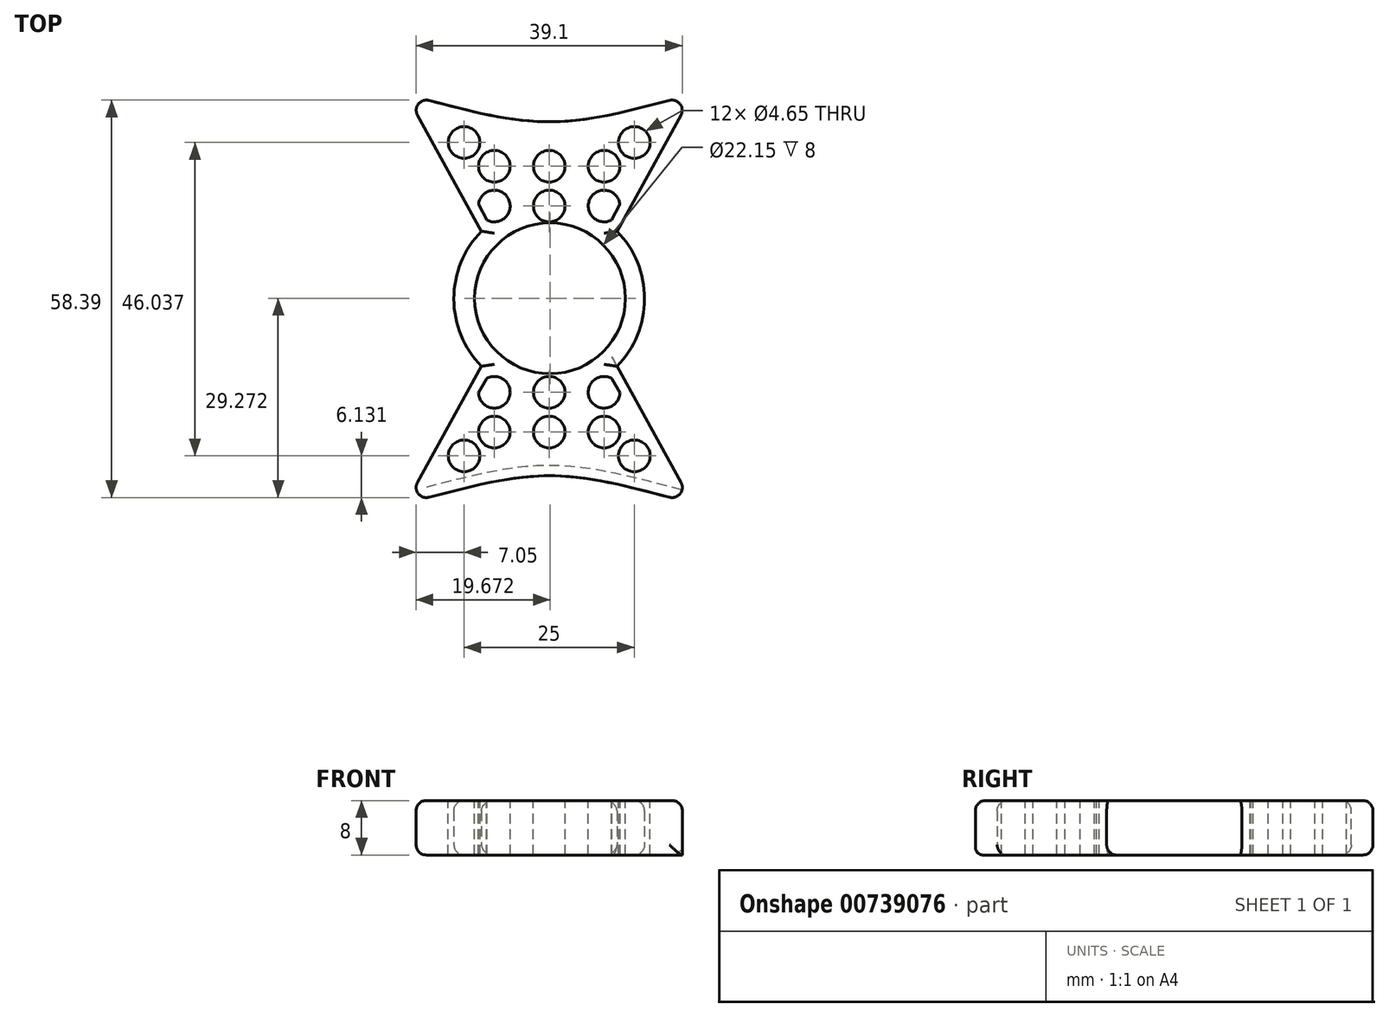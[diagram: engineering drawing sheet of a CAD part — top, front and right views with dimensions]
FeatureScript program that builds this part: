
annotation { "Feature Type Name" : "Feature", "Feature Type Description" : "" }
export const myFeature = defineFeature(function(context is Context, id is Id, definition is map)
    precondition{}
    {
        {
            var Q0;
            Q0=qCreatedBy(makeId("Top.planeOp"),FACE);
            var sketch = newSketch(context, id + "F0", { "sketchPlane" : qUnion([Q0])});
            skCircle(sketch, "E0", {"center": v(0, 0) * mm, "radius": 14 * mm});
            skLineSegment(sketch, "E1", {"start": v(-14, 0) * mm, "end": v(0, 0) * mm});
            skLineSegment(sketch, "E2", {"start": v(-9.9, 9.9) * mm, "end": v(0, 0) * mm});
            skLineSegment(sketch, "E3", {"start": v(9.9, 9.9) * mm, "end": v(0, 0) * mm});
            skLineSegment(sketch, "E4", {"start": v(0, 0) * mm, "end": v(14, 0) * mm});
            skLineSegment(sketch, "E5", {"start": v(-9.9, 9.9) * mm, "end": v(-21.01, 30.04) * mm});
            skLineSegment(sketch, "E6", {"start": v(9.9, 9.9) * mm, "end": v(21.01, 30.04) * mm});
            skFitSpline(sketch, "E7", {"points": [v(-21.01, 30.04) * mm, v(0, 26.06) * mm, v(21.01, 30.04) * mm], "startDerivative": vector(39.9, -9.48) * mm, "endDerivative": vector(39.9, 9.48) * mm});
            skCircle(sketch, "E8.1.0", {"center": v(0, 0.12) * mm, "radius": 14 * mm});
            skLineSegment(sketch, "E8.1.1", {"start": v(14, 0.12) * mm, "end": v(0, 0.12) * mm});
            skLineSegment(sketch, "E8.1.2", {"start": v(-9.9, -9.78) * mm, "end": v(-21.01, -29.91) * mm});
            skLineSegment(sketch, "E8.1.3", {"start": v(9.9, -9.78) * mm, "end": v(21.01, -29.91) * mm});
            skLineSegment(sketch, "E8.1.4", {"start": v(9.9, -9.78) * mm, "end": v(0, 0.12) * mm});
            skLineSegment(sketch, "E8.1.5", {"start": v(-9.9, -9.78) * mm, "end": v(0, 0.12) * mm});
            skLineSegment(sketch, "E8.1.6", {"start": v(0, 0.12) * mm, "end": v(-14, 0.12) * mm});
            skPoint(sketch, "E8.center", {"position": v(0, 0.06) * mm});
            skFitSpline(sketch, "E9", {"points": [v(-21.01, -29.91) * mm, v(0, -25.94) * mm, v(21.01, -29.91) * mm], "startDerivative": vector(39.9, 9.1) * mm, "endDerivative": vector(39.9, -9.1) * mm});
            skSolve(sketch);
        }
        {
            var Q0;
            Q0 = qSketchRegion(id + "F0", true);
            var Q1;
            {var subQ1=sQuery(id+"F0.wireOp",EDGE,"E0");var subQ3=sQuery(id+"F0.wireOp",EDGE,"E8.1.1");var subQ4=makeQuery(id+"F0.imprint","INTERSECT",VERTEX,{"derivedFrom":[subQ1,subQ3]});Q1=makeQuery(id+"F0.imprint","IMPRINT",FACE,{"disambiguationData":[TD([[makeQuery(id+"F0.imprint","IMPRINT",EDGE,{"disambiguationData":[TD([[subQ4,-1.0]])],"derivedFrom":subQ3}),-1.0]])]});}
            var Q2;
            {var subQ0=sQuery(id+"F0.wireOp",EDGE,"E8.1.6");var subQ5=sQuery(id+"F0.wireOp",EDGE,"E2");var subQ6=makeQuery(id+"F0.imprint","INTERSECT",VERTEX,{"derivedFrom":[subQ5,subQ0]});Q2=makeQuery(id+"F0.imprint","IMPRINT",FACE,{"disambiguationData":[TD([[makeQuery(id+"F0.imprint","IMPRINT",EDGE,{"disambiguationData":[TD([[subQ6,1.0]])],"derivedFrom":subQ5}),1.0]])]});}
            var Q3;
            {var subQ1=sQuery(id+"F0.wireOp",EDGE,"E0");var subQ3=sQuery(id+"F0.wireOp",EDGE,"E8.1.6");var subQ4=makeQuery(id+"F0.imprint","INTERSECT",VERTEX,{"derivedFrom":[subQ1,subQ3]});Q3=makeQuery(id+"F0.imprint","IMPRINT",FACE,{"disambiguationData":[TD([[makeQuery(id+"F0.imprint","IMPRINT",EDGE,{"disambiguationData":[TD([[subQ4,1.0]])],"derivedFrom":subQ3}),-1.0]])]});}
            var Q4;
            {var subQ0=sQuery(id+"F0.wireOp",EDGE,"E8.1.0");var subQ1=sQuery(id+"F0.wireOp",EDGE,"E1");var subQ2=makeQuery(id+"F0.imprint","INTERSECT",VERTEX,{"derivedFrom":[subQ1,subQ0]});Q4=makeQuery(id+"F0.imprint","IMPRINT",FACE,{"disambiguationData":[TD([[makeQuery(id+"F0.imprint","IMPRINT",EDGE,{"disambiguationData":[TD([[subQ2,-1.0]])],"derivedFrom":subQ1}),-1.0]])]});}
            var Q5;
            {var subQ0=sQuery(id+"F0.wireOp",EDGE,"E8.1.4");var subQ1=sQuery(id+"F0.wireOp",EDGE,"E4");var subQ2=makeQuery(id+"F0.imprint","INTERSECT",VERTEX,{"derivedFrom":[subQ1,subQ0]});Q5=makeQuery(id+"F0.imprint","IMPRINT",FACE,{"disambiguationData":[TD([[makeQuery(id+"F0.imprint","IMPRINT",EDGE,{"disambiguationData":[TD([[subQ2,-1.0]])],"derivedFrom":subQ1}),-1.0]])]});}
            var Q6;
            {var subQ3=sQuery(id+"F0.wireOp",EDGE,"E8.1.4");var subQ5=sQuery(id+"F0.wireOp",EDGE,"E4");var subQ8=makeQuery(id+"F0.imprint","INTERSECT",VERTEX,{"derivedFrom":[subQ5,subQ3]});Q6=makeQuery(id+"F0.imprint","IMPRINT",FACE,{"disambiguationData":[TD([[makeQuery(id+"F0.imprint","IMPRINT",EDGE,{"disambiguationData":[TD([[subQ8,1.0]])],"derivedFrom":subQ3}),1.0]])]});}
            extrude(context, id + "F1", {"entities" : qUnion([Q0, Q1, Q2, Q3, Q4, Q5, Q6]), "depth" : 8 * mm, "offsetDistance" : 25 * mm});
        }
        {
            var Q0;
            Q0=makeQuery(id+"F1.opExtrude","SWEPT_EDGE",EDGE,{"disambiguationData":[OSD([sQuery(id+"F0.wireOp",EDGE,"E8.1.2"),sQuery(id+"F0.wireOp",EDGE,"E9")])]});
            var Q1;
            Q1=makeQuery(id+"F1.opExtrude","CAP_EDGE",EDGE,{"disambiguationData":[OSD([sQuery(id+"F0.wireOp",EDGE,"E9")])],"isStart":true});
            var Q2;
            Q2=makeQuery(id+"F1.opExtrude","CAP_EDGE",EDGE,{"disambiguationData":[OSD([sQuery(id+"F0.wireOp",EDGE,"E9")])],"isStart":false});
            var Q3;
            Q3=makeQuery(id+"F1.opExtrude","CAP_EDGE",EDGE,{"disambiguationData":[OSD([sQuery(id+"F0.wireOp",EDGE,"E8.1.2")])],"isStart":false});
            var Q4;
            {var subQ0=sQuery(id+"F0.wireOp",EDGE,"E0");var subQ1=makeQuery(id+"F0.imprint","INTERSECT",VERTEX,{"derivedFrom":[subQ0,sQuery(id+"F0.wireOp",EDGE,"E1")]});Q4=makeQuery(id+"F1.opExtrude","CAP_EDGE",EDGE,{"disambiguationData":[OSD([subQ0]),TDD([makeQuery(id+"F0.imprint","IMPRINT",EDGE,{"disambiguationData":[TD([[subQ1,1.0]])],"derivedFrom":subQ0}),makeQuery(id+"F0.imprint","IMPRINT",EDGE,{"disambiguationData":[TD([[subQ1,-1.0]])],"derivedFrom":subQ0})])],"isStart":false});}
            var Q5;
            {var subQ0=sQuery(id+"F0.wireOp",EDGE,"E8.1.0");var subQ1=makeQuery(id+"F0.imprint","INTERSECT",VERTEX,{"derivedFrom":[subQ0,sQuery(id+"F0.wireOp",EDGE,"E8.1.6")]});Q5=makeQuery(id+"F1.opExtrude","CAP_EDGE",EDGE,{"disambiguationData":[OSD([subQ0]),TDD([makeQuery(id+"F0.imprint","IMPRINT",EDGE,{"disambiguationData":[TD([[subQ1,-1.0]])],"derivedFrom":subQ0}),makeQuery(id+"F0.imprint","IMPRINT",EDGE,{"disambiguationData":[TD([[subQ1,1.0]])],"derivedFrom":subQ0})])],"isStart":false});}
            var Q6;
            Q6=makeQuery(id+"F1.opExtrude","CAP_EDGE",EDGE,{"disambiguationData":[OSD([sQuery(id+"F0.wireOp",EDGE,"E5")])],"isStart":false});
            var Q7;
            Q7=makeQuery(id+"F1.opExtrude","CAP_EDGE",EDGE,{"disambiguationData":[OSD([sQuery(id+"F0.wireOp",EDGE,"E7")])],"isStart":false});
            var Q8;
            Q8=makeQuery(id+"F1.opExtrude","CAP_EDGE",EDGE,{"disambiguationData":[OSD([sQuery(id+"F0.wireOp",EDGE,"E6")])],"isStart":false});
            var Q9;
            Q9=makeQuery(id+"F1.opExtrude","SWEPT_EDGE",EDGE,{"disambiguationData":[OSD([sQuery(id+"F0.wireOp",EDGE,"E6"),sQuery(id+"F0.wireOp",EDGE,"E7")])]});
            var Q10;
            Q10=makeQuery(id+"F1.opExtrude","CAP_EDGE",EDGE,{"disambiguationData":[OSD([sQuery(id+"F0.wireOp",EDGE,"E6")])],"isStart":true});
            var Q11;
            {var subQ0=sQuery(id+"F0.wireOp",EDGE,"E0");var subQ1=makeQuery(id+"F0.imprint","INTERSECT",VERTEX,{"derivedFrom":[subQ0,sQuery(id+"F0.wireOp",EDGE,"E4")]});Q11=makeQuery(id+"F1.opExtrude","CAP_EDGE",EDGE,{"disambiguationData":[OSD([subQ0]),TDD([makeQuery(id+"F0.imprint","IMPRINT",EDGE,{"disambiguationData":[TD([[subQ1,-1.0]])],"derivedFrom":subQ0}),makeQuery(id+"F0.imprint","IMPRINT",EDGE,{"disambiguationData":[TD([[subQ1,1.0]])],"derivedFrom":subQ0})])],"isStart":true});}
            var Q12;
            {var subQ0=sQuery(id+"F0.wireOp",EDGE,"E8.1.0");var subQ1=makeQuery(id+"F0.imprint","INTERSECT",VERTEX,{"derivedFrom":[subQ0,sQuery(id+"F0.wireOp",EDGE,"E8.1.1")]});Q12=makeQuery(id+"F1.opExtrude","CAP_EDGE",EDGE,{"disambiguationData":[OSD([subQ0]),TDD([makeQuery(id+"F0.imprint","IMPRINT",EDGE,{"disambiguationData":[TD([[subQ1,1.0]])],"derivedFrom":subQ0}),makeQuery(id+"F0.imprint","IMPRINT",EDGE,{"disambiguationData":[TD([[subQ1,-1.0]])],"derivedFrom":subQ0})])],"isStart":true});}
            var Q13;
            {var subQ0=sQuery(id+"F0.wireOp",EDGE,"E8.1.0");var subQ1=makeQuery(id+"F0.imprint","INTERSECT",VERTEX,{"derivedFrom":[subQ0,sQuery(id+"F0.wireOp",EDGE,"E8.1.1")]});Q13=makeQuery(id+"F1.opExtrude","CAP_EDGE",EDGE,{"disambiguationData":[OSD([subQ0]),TDD([makeQuery(id+"F0.imprint","IMPRINT",EDGE,{"disambiguationData":[TD([[subQ1,1.0]])],"derivedFrom":subQ0}),makeQuery(id+"F0.imprint","IMPRINT",EDGE,{"disambiguationData":[TD([[subQ1,-1.0]])],"derivedFrom":subQ0})])],"isStart":false});}
            var Q14;
            Q14=makeQuery(id+"F1.opExtrude","CAP_EDGE",EDGE,{"disambiguationData":[OSD([sQuery(id+"F0.wireOp",EDGE,"E8.1.3")])],"isStart":false});
            var Q15;
            {var subQ0=sQuery(id+"F0.wireOp",EDGE,"E0");var subQ1=makeQuery(id+"F0.imprint","INTERSECT",VERTEX,{"derivedFrom":[subQ0,sQuery(id+"F0.wireOp",EDGE,"E4")]});Q15=makeQuery(id+"F1.opExtrude","CAP_EDGE",EDGE,{"disambiguationData":[OSD([subQ0]),TDD([makeQuery(id+"F0.imprint","IMPRINT",EDGE,{"disambiguationData":[TD([[subQ1,-1.0]])],"derivedFrom":subQ0}),makeQuery(id+"F0.imprint","IMPRINT",EDGE,{"disambiguationData":[TD([[subQ1,1.0]])],"derivedFrom":subQ0})])],"isStart":false});}
            var Q16;
            Q16=makeQuery(id+"F1.opExtrude","CAP_EDGE",EDGE,{"disambiguationData":[OSD([sQuery(id+"F0.wireOp",EDGE,"E5")])],"isStart":true});
            var Q17;
            Q17=makeQuery(id+"F1.opExtrude","CAP_EDGE",EDGE,{"disambiguationData":[OSD([sQuery(id+"F0.wireOp",EDGE,"E7")])],"isStart":true});
            var Q18;
            {var subQ0=sQuery(id+"F0.wireOp",EDGE,"E8.1.0");var subQ1=makeQuery(id+"F0.imprint","INTERSECT",VERTEX,{"derivedFrom":[subQ0,sQuery(id+"F0.wireOp",EDGE,"E8.1.6")]});Q18=makeQuery(id+"F1.opExtrude","CAP_EDGE",EDGE,{"disambiguationData":[OSD([subQ0]),TDD([makeQuery(id+"F0.imprint","IMPRINT",EDGE,{"disambiguationData":[TD([[subQ1,-1.0]])],"derivedFrom":subQ0}),makeQuery(id+"F0.imprint","IMPRINT",EDGE,{"disambiguationData":[TD([[subQ1,1.0]])],"derivedFrom":subQ0})])],"isStart":true});}
            var Q19;
            {var subQ0=sQuery(id+"F0.wireOp",EDGE,"E0");var subQ1=makeQuery(id+"F0.imprint","INTERSECT",VERTEX,{"derivedFrom":[subQ0,sQuery(id+"F0.wireOp",EDGE,"E1")]});Q19=makeQuery(id+"F1.opExtrude","CAP_EDGE",EDGE,{"disambiguationData":[OSD([subQ0]),TDD([makeQuery(id+"F0.imprint","IMPRINT",EDGE,{"disambiguationData":[TD([[subQ1,1.0]])],"derivedFrom":subQ0}),makeQuery(id+"F0.imprint","IMPRINT",EDGE,{"disambiguationData":[TD([[subQ1,-1.0]])],"derivedFrom":subQ0})])],"isStart":true});}
            var Q20;
            Q20=makeQuery(id+"F1.opExtrude","CAP_EDGE",EDGE,{"disambiguationData":[OSD([sQuery(id+"F0.wireOp",EDGE,"E8.1.2")])],"isStart":true});
            var Q21;
            Q21=makeQuery(id+"F1.opExtrude","SWEPT_EDGE",EDGE,{"disambiguationData":[OSD([sQuery(id+"F0.wireOp",EDGE,"E8.1.3"),sQuery(id+"F0.wireOp",EDGE,"E9")])]});
            var Q22;
            Q22=makeQuery(id+"F1.opExtrude","SWEPT_EDGE",EDGE,{"disambiguationData":[OSD([sQuery(id+"F0.wireOp",EDGE,"E5"),sQuery(id+"F0.wireOp",EDGE,"E7")])]});
            fillet(context, id + "F2", {"entities" : qUnion([Q0, Q1, Q2, Q3, Q4, Q5, Q6, Q7, Q8, Q9, Q10, Q11, Q12, Q13, Q14, Q15, Q16, Q17, Q18, Q19, Q20, Q21, Q22]), "radius" : 1.5 * mm, "tangentPropagation" : true, "allowEdgeOverflow" : false});
        }
        {
            var Q0;
            Q0=makeQuery(id+"F1.opExtrude","CAP_FACE",FACE,{"disambiguationData":[OSD([sQuery(id+"F0.wireOp",EDGE,"E0"),sQuery(id+"F0.wireOp",EDGE,"E1"),sQuery(id+"F0.wireOp",EDGE,"E2"),sQuery(id+"F0.wireOp",EDGE,"E3"),sQuery(id+"F0.wireOp",EDGE,"E4"),sQuery(id+"F0.wireOp",EDGE,"E5"),sQuery(id+"F0.wireOp",EDGE,"E6"),sQuery(id+"F0.wireOp",EDGE,"E7"),sQuery(id+"F0.wireOp",EDGE,"E8.1.0"),sQuery(id+"F0.wireOp",EDGE,"E8.1.1"),sQuery(id+"F0.wireOp",EDGE,"E8.1.2"),sQuery(id+"F0.wireOp",EDGE,"E8.1.3"),sQuery(id+"F0.wireOp",EDGE,"E8.1.4"),sQuery(id+"F0.wireOp",EDGE,"E8.1.5"),sQuery(id+"F0.wireOp",EDGE,"E8.1.6"),sQuery(id+"F0.wireOp",EDGE,"E9")])],"isStart":false});
            var sketch = newSketch(context, id + "F3", { "sketchPlane" : qUnion([Q0])});
            skCircle(sketch, "E10", {"center": v(0.12, 0.12) * mm, "radius": 11.07 * mm});
            skCircle(sketch, "E11", {"center": v(0, -13.68) * mm, "radius": 2.33 * mm});
            skCircle(sketch, "E12", {"center": v(0, -19.52) * mm, "radius": 2.33 * mm});
            skCircle(sketch, "E13", {"center": v(8.06, -19.52) * mm, "radius": 2.33 * mm});
            skCircle(sketch, "E14", {"center": v(-8.06, -19.52) * mm, "radius": 2.33 * mm});
            skCircle(sketch, "E15", {"center": v(-8.06, -13.68) * mm, "radius": 2.33 * mm});
            skCircle(sketch, "E16", {"center": v(8.06, -13.68) * mm, "radius": 2.33 * mm});
            skCircle(sketch, "E17", {"center": v(-12.5, -23.02) * mm, "radius": 2.33 * mm});
            skPoint(sketch, "E18.centerSnap0", {"position": v(11.35, -5.24) * mm});
            skCircle(sketch, "E19", {"center": v(12.5, -23.02) * mm, "radius": 2.33 * mm});
            skCircle(sketch, "E20.1.0", {"center": v(0, 19.52) * mm, "radius": 2.33 * mm});
            skCircle(sketch, "E20.1.1", {"center": v(8.06, 19.52) * mm, "radius": 2.33 * mm});
            skCircle(sketch, "E20.1.2", {"center": v(12.5, 23.02) * mm, "radius": 2.33 * mm});
            skCircle(sketch, "E20.1.3", {"center": v(8.06, 13.68) * mm, "radius": 2.33 * mm});
            skCircle(sketch, "E20.1.4", {"center": v(0, 13.68) * mm, "radius": 2.33 * mm});
            skCircle(sketch, "E20.1.5", {"center": v(-8.06, 13.68) * mm, "radius": 2.33 * mm});
            skCircle(sketch, "E20.1.6", {"center": v(-8.06, 19.52) * mm, "radius": 2.33 * mm});
            skCircle(sketch, "E20.1.7", {"center": v(-12.5, 23.02) * mm, "radius": 2.33 * mm});
            skPoint(sketch, "E20.center", {"position": v(0, 0) * mm});
            skSolve(sketch);
        }
        {
            var Q0;
            Q0=makeQuery(id+"F3.imprint","IMPRINT",FACE,{"disambiguationData":[TD([[makeQuery(id+"F3.imprint","IMPRINT",EDGE,{"derivedFrom":sQuery(id+"F3.wireOp",EDGE,"E17")}),1.0]])]});
            var Q1;
            Q1=makeQuery(id+"F3.imprint","IMPRINT",FACE,{"disambiguationData":[TD([[makeQuery(id+"F3.imprint","IMPRINT",EDGE,{"derivedFrom":sQuery(id+"F3.wireOp",EDGE,"E14")}),1.0]])]});
            var Q2;
            {var subQ0=sQuery(id+"F3.wireOp",EDGE,"E15");var subQ1=sQuery(id+"F0.wireOp",EDGE,"E8.1.2");var subQ2=makeQuery(id+"F2.opFillet","BLEND_EDGE",EDGE,{"blendedFrom":[makeQuery(id+"F1.opExtrude","CAP_EDGE",EDGE,{"disambiguationData":[OSD([subQ1])],"isStart":false}),makeQuery(id+"F1.opExtrude","CAP_FACE",FACE,{"disambiguationData":[OSD([sQuery(id+"F0.wireOp",EDGE,"E0"),sQuery(id+"F0.wireOp",EDGE,"E1"),sQuery(id+"F0.wireOp",EDGE,"E2"),sQuery(id+"F0.wireOp",EDGE,"E3"),sQuery(id+"F0.wireOp",EDGE,"E4"),sQuery(id+"F0.wireOp",EDGE,"E5"),sQuery(id+"F0.wireOp",EDGE,"E6"),sQuery(id+"F0.wireOp",EDGE,"E7"),sQuery(id+"F0.wireOp",EDGE,"E8.1.0"),sQuery(id+"F0.wireOp",EDGE,"E8.1.1"),subQ1,sQuery(id+"F0.wireOp",EDGE,"E8.1.3"),sQuery(id+"F0.wireOp",EDGE,"E8.1.4"),sQuery(id+"F0.wireOp",EDGE,"E8.1.5"),sQuery(id+"F0.wireOp",EDGE,"E8.1.6"),sQuery(id+"F0.wireOp",EDGE,"E9")])],"isStart":false})],"blendedInto":[makeQuery(id+"F1.opExtrude","CAP_FACE",FACE,{"disambiguationData":[OSD([sQuery(id+"F0.wireOp",EDGE,"E0"),sQuery(id+"F0.wireOp",EDGE,"E1"),sQuery(id+"F0.wireOp",EDGE,"E2"),sQuery(id+"F0.wireOp",EDGE,"E3"),sQuery(id+"F0.wireOp",EDGE,"E4"),sQuery(id+"F0.wireOp",EDGE,"E5"),sQuery(id+"F0.wireOp",EDGE,"E6"),sQuery(id+"F0.wireOp",EDGE,"E7"),sQuery(id+"F0.wireOp",EDGE,"E8.1.0"),sQuery(id+"F0.wireOp",EDGE,"E8.1.1"),subQ1,sQuery(id+"F0.wireOp",EDGE,"E8.1.3"),sQuery(id+"F0.wireOp",EDGE,"E8.1.4"),sQuery(id+"F0.wireOp",EDGE,"E8.1.5"),sQuery(id+"F0.wireOp",EDGE,"E8.1.6"),sQuery(id+"F0.wireOp",EDGE,"E9")])],"isStart":false})]});var subQ3=makeQuery(id+"F3.imprint","INTERSECT",VERTEX,{"disambiguationData":[OD(0.0)],"derivedFrom":[subQ2,subQ0]});Q2=makeQuery(id+"F3.imprint","IMPRINT",FACE,{"disambiguationData":[TD([[makeQuery(id+"F3.imprint","IMPRINT",EDGE,{"disambiguationData":[TD([[subQ3,-1.0]])],"derivedFrom":subQ0}),1.0]])]});}
            var Q3;
            Q3=makeQuery(id+"F3.imprint","IMPRINT",FACE,{"disambiguationData":[TD([[makeQuery(id+"F3.imprint","IMPRINT",EDGE,{"derivedFrom":sQuery(id+"F3.wireOp",EDGE,"E12")}),1.0]])]});
            var Q4;
            Q4=makeQuery(id+"F3.imprint","IMPRINT",FACE,{"disambiguationData":[TD([[makeQuery(id+"F3.imprint","IMPRINT",EDGE,{"derivedFrom":sQuery(id+"F3.wireOp",EDGE,"E11")}),1.0]])]});
            var Q5;
            {var subQ0=sQuery(id+"F3.wireOp",EDGE,"E16");var subQ1=sQuery(id+"F0.wireOp",EDGE,"E8.1.3");var subQ2=makeQuery(id+"F2.opFillet","BLEND_EDGE",EDGE,{"blendedFrom":[makeQuery(id+"F1.opExtrude","CAP_EDGE",EDGE,{"disambiguationData":[OSD([subQ1])],"isStart":false}),makeQuery(id+"F1.opExtrude","CAP_FACE",FACE,{"disambiguationData":[OSD([sQuery(id+"F0.wireOp",EDGE,"E0"),sQuery(id+"F0.wireOp",EDGE,"E1"),sQuery(id+"F0.wireOp",EDGE,"E2"),sQuery(id+"F0.wireOp",EDGE,"E3"),sQuery(id+"F0.wireOp",EDGE,"E4"),sQuery(id+"F0.wireOp",EDGE,"E5"),sQuery(id+"F0.wireOp",EDGE,"E6"),sQuery(id+"F0.wireOp",EDGE,"E7"),sQuery(id+"F0.wireOp",EDGE,"E8.1.0"),sQuery(id+"F0.wireOp",EDGE,"E8.1.1"),sQuery(id+"F0.wireOp",EDGE,"E8.1.2"),subQ1,sQuery(id+"F0.wireOp",EDGE,"E8.1.4"),sQuery(id+"F0.wireOp",EDGE,"E8.1.5"),sQuery(id+"F0.wireOp",EDGE,"E8.1.6"),sQuery(id+"F0.wireOp",EDGE,"E9")])],"isStart":false})],"blendedInto":[makeQuery(id+"F1.opExtrude","CAP_FACE",FACE,{"disambiguationData":[OSD([sQuery(id+"F0.wireOp",EDGE,"E0"),sQuery(id+"F0.wireOp",EDGE,"E1"),sQuery(id+"F0.wireOp",EDGE,"E2"),sQuery(id+"F0.wireOp",EDGE,"E3"),sQuery(id+"F0.wireOp",EDGE,"E4"),sQuery(id+"F0.wireOp",EDGE,"E5"),sQuery(id+"F0.wireOp",EDGE,"E6"),sQuery(id+"F0.wireOp",EDGE,"E7"),sQuery(id+"F0.wireOp",EDGE,"E8.1.0"),sQuery(id+"F0.wireOp",EDGE,"E8.1.1"),sQuery(id+"F0.wireOp",EDGE,"E8.1.2"),subQ1,sQuery(id+"F0.wireOp",EDGE,"E8.1.4"),sQuery(id+"F0.wireOp",EDGE,"E8.1.5"),sQuery(id+"F0.wireOp",EDGE,"E8.1.6"),sQuery(id+"F0.wireOp",EDGE,"E9")])],"isStart":false})]});var subQ3=makeQuery(id+"F3.imprint","INTERSECT",VERTEX,{"disambiguationData":[OD(0.0)],"derivedFrom":[subQ2,subQ0]});Q5=makeQuery(id+"F3.imprint","IMPRINT",FACE,{"disambiguationData":[TD([[makeQuery(id+"F3.imprint","IMPRINT",EDGE,{"disambiguationData":[TD([[subQ3,1.0]])],"derivedFrom":subQ0}),1.0]])]});}
            var Q6;
            Q6=makeQuery(id+"F3.imprint","IMPRINT",FACE,{"disambiguationData":[TD([[makeQuery(id+"F3.imprint","IMPRINT",EDGE,{"derivedFrom":sQuery(id+"F3.wireOp",EDGE,"E13")}),1.0]])]});
            var Q7;
            Q7=makeQuery(id+"F3.imprint","IMPRINT",FACE,{"disambiguationData":[TD([[makeQuery(id+"F3.imprint","IMPRINT",EDGE,{"derivedFrom":sQuery(id+"F3.wireOp",EDGE,"E19")}),1.0]])]});
            var Q8;
            {var subQ0=sQuery(id+"F3.wireOp",EDGE,"E20.1.5");var subQ1=sQuery(id+"F0.wireOp",EDGE,"E5");var subQ2=makeQuery(id+"F2.opFillet","BLEND_EDGE",EDGE,{"blendedFrom":[makeQuery(id+"F1.opExtrude","CAP_EDGE",EDGE,{"disambiguationData":[OSD([subQ1])],"isStart":false}),makeQuery(id+"F1.opExtrude","CAP_FACE",FACE,{"disambiguationData":[OSD([sQuery(id+"F0.wireOp",EDGE,"E0"),sQuery(id+"F0.wireOp",EDGE,"E1"),sQuery(id+"F0.wireOp",EDGE,"E2"),sQuery(id+"F0.wireOp",EDGE,"E3"),sQuery(id+"F0.wireOp",EDGE,"E4"),subQ1,sQuery(id+"F0.wireOp",EDGE,"E6"),sQuery(id+"F0.wireOp",EDGE,"E7"),sQuery(id+"F0.wireOp",EDGE,"E8.1.0"),sQuery(id+"F0.wireOp",EDGE,"E8.1.1"),sQuery(id+"F0.wireOp",EDGE,"E8.1.2"),sQuery(id+"F0.wireOp",EDGE,"E8.1.3"),sQuery(id+"F0.wireOp",EDGE,"E8.1.4"),sQuery(id+"F0.wireOp",EDGE,"E8.1.5"),sQuery(id+"F0.wireOp",EDGE,"E8.1.6"),sQuery(id+"F0.wireOp",EDGE,"E9")])],"isStart":false})],"blendedInto":[makeQuery(id+"F1.opExtrude","CAP_FACE",FACE,{"disambiguationData":[OSD([sQuery(id+"F0.wireOp",EDGE,"E0"),sQuery(id+"F0.wireOp",EDGE,"E1"),sQuery(id+"F0.wireOp",EDGE,"E2"),sQuery(id+"F0.wireOp",EDGE,"E3"),sQuery(id+"F0.wireOp",EDGE,"E4"),subQ1,sQuery(id+"F0.wireOp",EDGE,"E6"),sQuery(id+"F0.wireOp",EDGE,"E7"),sQuery(id+"F0.wireOp",EDGE,"E8.1.0"),sQuery(id+"F0.wireOp",EDGE,"E8.1.1"),sQuery(id+"F0.wireOp",EDGE,"E8.1.2"),sQuery(id+"F0.wireOp",EDGE,"E8.1.3"),sQuery(id+"F0.wireOp",EDGE,"E8.1.4"),sQuery(id+"F0.wireOp",EDGE,"E8.1.5"),sQuery(id+"F0.wireOp",EDGE,"E8.1.6"),sQuery(id+"F0.wireOp",EDGE,"E9")])],"isStart":false})]});var subQ3=makeQuery(id+"F3.imprint","INTERSECT",VERTEX,{"disambiguationData":[OD(0.0)],"derivedFrom":[subQ2,subQ0]});Q8=makeQuery(id+"F3.imprint","IMPRINT",FACE,{"disambiguationData":[TD([[makeQuery(id+"F3.imprint","IMPRINT",EDGE,{"disambiguationData":[TD([[subQ3,1.0]])],"derivedFrom":subQ0}),1.0]])]});}
            var Q9;
            Q9=makeQuery(id+"F3.imprint","IMPRINT",FACE,{"disambiguationData":[TD([[makeQuery(id+"F3.imprint","IMPRINT",EDGE,{"derivedFrom":sQuery(id+"F3.wireOp",EDGE,"E20.1.6")}),1.0]])]});
            var Q10;
            Q10=makeQuery(id+"F3.imprint","IMPRINT",FACE,{"disambiguationData":[TD([[makeQuery(id+"F3.imprint","IMPRINT",EDGE,{"derivedFrom":sQuery(id+"F3.wireOp",EDGE,"E20.1.7")}),1.0]])]});
            var Q11;
            Q11=makeQuery(id+"F3.imprint","IMPRINT",FACE,{"disambiguationData":[TD([[makeQuery(id+"F3.imprint","IMPRINT",EDGE,{"derivedFrom":sQuery(id+"F3.wireOp",EDGE,"E20.1.0")}),1.0]])]});
            var Q12;
            Q12=makeQuery(id+"F3.imprint","IMPRINT",FACE,{"disambiguationData":[TD([[makeQuery(id+"F3.imprint","IMPRINT",EDGE,{"derivedFrom":sQuery(id+"F3.wireOp",EDGE,"E20.1.4")}),1.0]])]});
            var Q13;
            {var subQ0=sQuery(id+"F3.wireOp",EDGE,"E20.1.3");var subQ1=sQuery(id+"F0.wireOp",EDGE,"E6");var subQ2=makeQuery(id+"F2.opFillet","BLEND_EDGE",EDGE,{"blendedFrom":[makeQuery(id+"F1.opExtrude","CAP_EDGE",EDGE,{"disambiguationData":[OSD([subQ1])],"isStart":false}),makeQuery(id+"F1.opExtrude","CAP_FACE",FACE,{"disambiguationData":[OSD([sQuery(id+"F0.wireOp",EDGE,"E0"),sQuery(id+"F0.wireOp",EDGE,"E1"),sQuery(id+"F0.wireOp",EDGE,"E2"),sQuery(id+"F0.wireOp",EDGE,"E3"),sQuery(id+"F0.wireOp",EDGE,"E4"),sQuery(id+"F0.wireOp",EDGE,"E5"),subQ1,sQuery(id+"F0.wireOp",EDGE,"E7"),sQuery(id+"F0.wireOp",EDGE,"E8.1.0"),sQuery(id+"F0.wireOp",EDGE,"E8.1.1"),sQuery(id+"F0.wireOp",EDGE,"E8.1.2"),sQuery(id+"F0.wireOp",EDGE,"E8.1.3"),sQuery(id+"F0.wireOp",EDGE,"E8.1.4"),sQuery(id+"F0.wireOp",EDGE,"E8.1.5"),sQuery(id+"F0.wireOp",EDGE,"E8.1.6"),sQuery(id+"F0.wireOp",EDGE,"E9")])],"isStart":false})],"blendedInto":[makeQuery(id+"F1.opExtrude","CAP_FACE",FACE,{"disambiguationData":[OSD([sQuery(id+"F0.wireOp",EDGE,"E0"),sQuery(id+"F0.wireOp",EDGE,"E1"),sQuery(id+"F0.wireOp",EDGE,"E2"),sQuery(id+"F0.wireOp",EDGE,"E3"),sQuery(id+"F0.wireOp",EDGE,"E4"),sQuery(id+"F0.wireOp",EDGE,"E5"),subQ1,sQuery(id+"F0.wireOp",EDGE,"E7"),sQuery(id+"F0.wireOp",EDGE,"E8.1.0"),sQuery(id+"F0.wireOp",EDGE,"E8.1.1"),sQuery(id+"F0.wireOp",EDGE,"E8.1.2"),sQuery(id+"F0.wireOp",EDGE,"E8.1.3"),sQuery(id+"F0.wireOp",EDGE,"E8.1.4"),sQuery(id+"F0.wireOp",EDGE,"E8.1.5"),sQuery(id+"F0.wireOp",EDGE,"E8.1.6"),sQuery(id+"F0.wireOp",EDGE,"E9")])],"isStart":false})]});var subQ3=makeQuery(id+"F3.imprint","INTERSECT",VERTEX,{"disambiguationData":[OD(0.0)],"derivedFrom":[subQ2,subQ0]});Q13=makeQuery(id+"F3.imprint","IMPRINT",FACE,{"disambiguationData":[TD([[makeQuery(id+"F3.imprint","IMPRINT",EDGE,{"disambiguationData":[TD([[subQ3,-1.0]])],"derivedFrom":subQ0}),1.0]])]});}
            var Q14;
            Q14=makeQuery(id+"F3.imprint","IMPRINT",FACE,{"disambiguationData":[TD([[makeQuery(id+"F3.imprint","IMPRINT",EDGE,{"derivedFrom":sQuery(id+"F3.wireOp",EDGE,"E20.1.1")}),1.0]])]});
            var Q15;
            Q15=makeQuery(id+"F3.imprint","IMPRINT",FACE,{"disambiguationData":[TD([[makeQuery(id+"F3.imprint","IMPRINT",EDGE,{"derivedFrom":sQuery(id+"F3.wireOp",EDGE,"E20.1.2")}),1.0]])]});
            var Q16;
            Q16=makeQuery(id+"F3.imprint","IMPRINT",FACE,{"disambiguationData":[TD([[makeQuery(id+"F3.imprint","IMPRINT",EDGE,{"derivedFrom":sQuery(id+"F3.wireOp",EDGE,"E10")}),1.0]])]});
            extrude(context, id + "F4", {"entities" : qUnion([Q0, Q1, Q2, Q3, Q4, Q5, Q6, Q7, Q8, Q9, Q10, Q11, Q12, Q13, Q14, Q15, Q16]), "operationType" : NewBodyOperationType.REMOVE, "oppositeDirection" : true, "depth" : 8 * mm, "offsetDistance" : 25 * mm});
        }
    });
